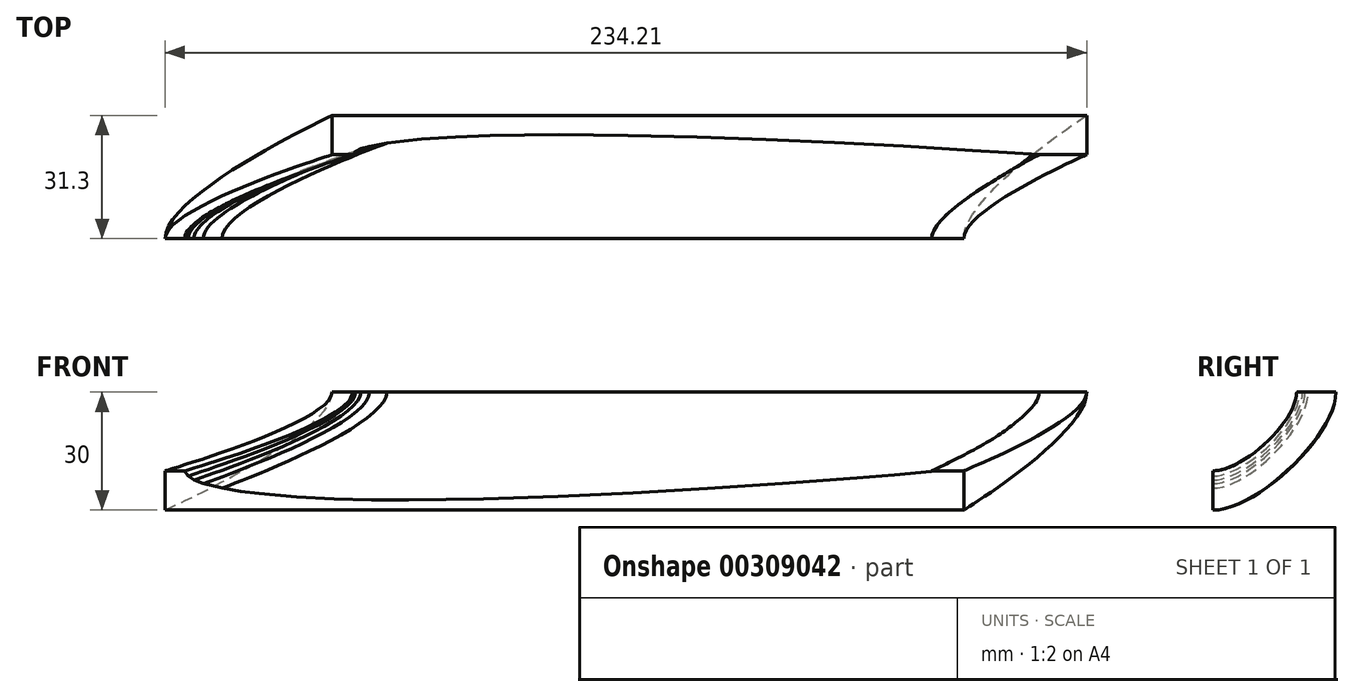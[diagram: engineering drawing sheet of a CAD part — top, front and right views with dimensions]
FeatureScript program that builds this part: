
annotation { "Feature Type Name" : "Feature", "Feature Type Description" : "" }
export const myFeature = defineFeature(function(context is Context, id is Id, definition is map)
    precondition{}
    {
        {
            var Q0;
            Q0=qCreatedBy(makeId("Top.planeOp"),FACE);
            cPlane(context, id + "F0", {"entities" : qUnion([Q0]), "cplaneType" : CPlaneType.OFFSET, "offset" : 20 * mm, "width" : 150 * mm, "height" : 150 * mm});
        }
        {
            var Q0;
            Q0=qCreatedBy(makeId("Front.planeOp"),FACE);
            var sketch = newSketch(context, id + "F1", { "sketchPlane" : qUnion([Q0])});
            skLineSegment(sketch, "E0", {"start": v(94.9, 0.16) * mm, "end": v(85.4, 1) * mm});
            skLineSegment(sketch, "E1", {"start": v(85.4, 1) * mm, "end": v(75.92, 1.8) * mm});
            skLineSegment(sketch, "E2", {"start": v(75.92, 1.8) * mm, "end": v(56.94, 3.25) * mm});
            skLineSegment(sketch, "E3", {"start": v(56.94, 3.25) * mm, "end": v(37.96, 4.54) * mm});
            skLineSegment(sketch, "E4", {"start": v(37.96, 4.54) * mm, "end": v(18.98, 5.66) * mm});
            skLineSegment(sketch, "E5", {"start": v(18.98, 5.66) * mm, "end": v(0, 6.56) * mm});
            skLineSegment(sketch, "E6", {"start": v(0, 6.56) * mm, "end": v(-18.98, 7.2) * mm});
            skLineSegment(sketch, "E7", {"start": v(-18.98, 7.2) * mm, "end": v(-37.96, 7.44) * mm});
            skLineSegment(sketch, "E8", {"start": v(-37.96, 7.44) * mm, "end": v(-47.45, 7.36) * mm});
            skLineSegment(sketch, "E9", {"start": v(-47.45, 7.36) * mm, "end": v(-56.94, 7.11) * mm});
            skLineSegment(sketch, "E10", {"start": v(-56.94, 7.11) * mm, "end": v(-66.43, 6.63) * mm});
            skLineSegment(sketch, "E11", {"start": v(-66.43, 6.63) * mm, "end": v(-75.92, 5.8) * mm});
            skLineSegment(sketch, "E12", {"start": v(-75.92, 5.8) * mm, "end": v(-80.66, 5.2) * mm});
            skLineSegment(sketch, "E13", {"start": v(-80.66, 5.2) * mm, "end": v(-85.4, 4.4) * mm});
            skLineSegment(sketch, "E14", {"start": v(-85.4, 4.4) * mm, "end": v(-90.15, 3.24) * mm});
            skLineSegment(sketch, "E15", {"start": v(-90.15, 3.24) * mm, "end": v(-92.52, 2.35) * mm});
            skLineSegment(sketch, "E16", {"start": v(-92.52, 2.35) * mm, "end": v(-94, 1.43) * mm});
            skLineSegment(sketch, "E17", {"start": v(-94, 1.43) * mm, "end": v(-94.9, 0) * mm});
            skLineSegment(sketch, "E18", {"start": v(-94.9, 0) * mm, "end": v(-94, -1.32) * mm});
            skLineSegment(sketch, "E19", {"start": v(-94, -1.32) * mm, "end": v(-92.52, -2.35) * mm});
            skLineSegment(sketch, "E20", {"start": v(-92.52, -2.35) * mm, "end": v(-90.15, -3.24) * mm});
            skLineSegment(sketch, "E21", {"start": v(-90.15, -3.24) * mm, "end": v(-85.4, -4.4) * mm});
            skLineSegment(sketch, "E22", {"start": v(-85.4, -4.4) * mm, "end": v(-80.66, -5.2) * mm});
            skLineSegment(sketch, "E23", {"start": v(-80.66, -5.2) * mm, "end": v(-75.92, -5.8) * mm});
            skLineSegment(sketch, "E24", {"start": v(-75.92, -5.8) * mm, "end": v(-66.43, -6.63) * mm});
            skLineSegment(sketch, "E25", {"start": v(-66.43, -6.63) * mm, "end": v(-56.94, -7.11) * mm});
            skLineSegment(sketch, "E26", {"start": v(-56.94, -7.11) * mm, "end": v(-47.45, -7.36) * mm});
            skLineSegment(sketch, "E27", {"start": v(-47.45, -7.36) * mm, "end": v(-37.96, -7.44) * mm});
            skLineSegment(sketch, "E28", {"start": v(-37.96, -7.44) * mm, "end": v(-18.98, -7.2) * mm});
            skLineSegment(sketch, "E29", {"start": v(-18.98, -7.2) * mm, "end": v(0, -6.56) * mm});
            skLineSegment(sketch, "E30", {"start": v(0, -6.56) * mm, "end": v(18.98, -5.66) * mm});
            skLineSegment(sketch, "E31", {"start": v(18.98, -5.66) * mm, "end": v(37.96, -4.54) * mm});
            skLineSegment(sketch, "E32", {"start": v(37.96, -4.54) * mm, "end": v(56.94, -3.25) * mm});
            skLineSegment(sketch, "E33", {"start": v(56.94, -3.25) * mm, "end": v(75.92, -1.8) * mm});
            skLineSegment(sketch, "E34", {"start": v(75.92, -1.8) * mm, "end": v(85.4, -1) * mm});
            skLineSegment(sketch, "E35", {"start": v(85.4, -1) * mm, "end": v(94.9, -0.16) * mm});
            skLineSegment(sketch, "E36", {"start": v(94.9, -0.16) * mm, "end": v(94.9, 0.16) * mm});
            skSolve(sketch);
        }
        {
            var Q0;
            Q0=qCreatedBy(id+"F0.planeOp",FACE);
            var sketch = newSketch(context, id + "F2", { "sketchPlane" : qUnion([Q0])});
            skLineSegment(sketch, "E37", {"start": v(122.76, 21.27) * mm, "end": v(114.01, 21.86) * mm});
            skLineSegment(sketch, "E38", {"start": v(114.01, 21.86) * mm, "end": v(105.26, 22.42) * mm});
            skLineSegment(sketch, "E39", {"start": v(105.26, 22.42) * mm, "end": v(87.76, 23.45) * mm});
            skLineSegment(sketch, "E40", {"start": v(87.76, 23.45) * mm, "end": v(70.26, 24.36) * mm});
            skLineSegment(sketch, "E41", {"start": v(70.26, 24.36) * mm, "end": v(52.76, 25.15) * mm});
            skLineSegment(sketch, "E42", {"start": v(52.76, 25.15) * mm, "end": v(35.26, 25.79) * mm});
            skLineSegment(sketch, "E43", {"start": v(35.26, 25.79) * mm, "end": v(17.76, 26.24) * mm});
            skLineSegment(sketch, "E44", {"start": v(17.76, 26.24) * mm, "end": v(0.26, 26.4) * mm});
            skLineSegment(sketch, "E45", {"start": v(0.26, 26.4) * mm, "end": v(-8.49, 26.36) * mm});
            skLineSegment(sketch, "E46", {"start": v(-8.49, 26.36) * mm, "end": v(-17.24, 26.18) * mm});
            skLineSegment(sketch, "E47", {"start": v(-17.24, 26.18) * mm, "end": v(-25.99, 25.83) * mm});
            skLineSegment(sketch, "E48", {"start": v(-25.99, 25.83) * mm, "end": v(-34.74, 25.25) * mm});
            skLineSegment(sketch, "E49", {"start": v(-34.74, 25.25) * mm, "end": v(-39.11, 24.83) * mm});
            skLineSegment(sketch, "E50", {"start": v(-39.11, 24.83) * mm, "end": v(-43.49, 24.27) * mm});
            skLineSegment(sketch, "E51", {"start": v(-43.49, 24.27) * mm, "end": v(-47.86, 23.44) * mm});
            skLineSegment(sketch, "E52", {"start": v(-47.86, 23.44) * mm, "end": v(-50.05, 22.81) * mm});
            skLineSegment(sketch, "E53", {"start": v(-50.05, 22.81) * mm, "end": v(-51.5, 22.08) * mm});
            skLineSegment(sketch, "E54", {"start": v(-51.5, 22.08) * mm, "end": v(-52.24, 21.16) * mm});
            skLineSegment(sketch, "E55", {"start": v(-52.24, 21.16) * mm, "end": v(-51.57, 20.22) * mm});
            skLineSegment(sketch, "E56", {"start": v(-51.57, 20.22) * mm, "end": v(-50.05, 19.5) * mm});
            skLineSegment(sketch, "E57", {"start": v(-50.05, 19.5) * mm, "end": v(-47.86, 18.87) * mm});
            skLineSegment(sketch, "E58", {"start": v(-47.86, 18.87) * mm, "end": v(-43.49, 18.05) * mm});
            skLineSegment(sketch, "E59", {"start": v(-43.49, 18.05) * mm, "end": v(-39.11, 17.48) * mm});
            skLineSegment(sketch, "E60", {"start": v(-39.11, 17.48) * mm, "end": v(-34.74, 17.06) * mm});
            skLineSegment(sketch, "E61", {"start": v(-34.74, 17.06) * mm, "end": v(-25.99, 16.48) * mm});
            skLineSegment(sketch, "E62", {"start": v(-25.99, 16.48) * mm, "end": v(-17.24, 16.14) * mm});
            skLineSegment(sketch, "E63", {"start": v(-17.24, 16.14) * mm, "end": v(-8.49, 15.96) * mm});
            skLineSegment(sketch, "E64", {"start": v(-8.49, 15.96) * mm, "end": v(0.26, 15.9) * mm});
            skLineSegment(sketch, "E65", {"start": v(0.26, 15.9) * mm, "end": v(17.76, 16.08) * mm});
            skLineSegment(sketch, "E66", {"start": v(17.76, 16.08) * mm, "end": v(35.26, 16.52) * mm});
            skLineSegment(sketch, "E67", {"start": v(35.26, 16.52) * mm, "end": v(52.76, 17.16) * mm});
            skLineSegment(sketch, "E68", {"start": v(52.76, 17.16) * mm, "end": v(70.26, 17.95) * mm});
            skLineSegment(sketch, "E69", {"start": v(70.26, 17.95) * mm, "end": v(87.76, 18.86) * mm});
            skLineSegment(sketch, "E70", {"start": v(87.76, 18.86) * mm, "end": v(105.26, 19.89) * mm});
            skLineSegment(sketch, "E71", {"start": v(105.26, 19.89) * mm, "end": v(114.01, 20.45) * mm});
            skLineSegment(sketch, "E72", {"start": v(114.01, 20.45) * mm, "end": v(122.76, 21.05) * mm});
            skLineSegment(sketch, "E73", {"start": v(122.76, 21.05) * mm, "end": v(122.76, 21.27) * mm});
            skSolve(sketch);
        }
        {
            var Q0;
            Q0=makeQuery(id+"F1.imprint","IMPRINT",FACE,{"disambiguationData":[TD([[makeQuery(id+"F1.imprint","IMPRINT",EDGE,{"derivedFrom":sQuery(id+"F1.wireOp",EDGE,"E0")}),1.0]])]});
            var Q1;
            Q1=makeQuery(id+"F2.imprint","IMPRINT",FACE,{"disambiguationData":[TD([[makeQuery(id+"F2.imprint","IMPRINT",EDGE,{"derivedFrom":sQuery(id+"F2.wireOp",EDGE,"E37")}),1.0]])]});
            loft(context, id + "F3", {"startCondition" : LoftEndDerivativeType.NORMAL_TO_PROFILE, "startMagnitude" : 1, "endCondition" : LoftEndDerivativeType.NORMAL_TO_PROFILE, "endMagnitude" : 1, "sheetProfilesArray" : [{ "sheetProfileEntities" : qUnion([Q0]) }, { "sheetProfileEntities" : qUnion([Q1]) }]});
        }
        {
            var Q0;
            Q0=qCreatedBy(makeId("Front.planeOp"),FACE);
            var sketch = newSketch(context, id + "F4", { "sketchPlane" : qUnion([Q0])});
            skLineSegment(sketch, "E74.bottom", {"start": v(-99.88, 0) * mm, "end": v(103.06, 0) * mm});
            skLineSegment(sketch, "E74.top", {"start": v(-99.88, -10) * mm, "end": v(103.06, -10) * mm});
            skLineSegment(sketch, "E74.left", {"start": v(-99.88, 0) * mm, "end": v(-99.88, -10) * mm});
            skLineSegment(sketch, "E74.right", {"start": v(103.06, 0) * mm, "end": v(103.06, -10) * mm});
            skSolve(sketch);
        }
        {
            var Q0;
            Q0=qCreatedBy(id+"F0.planeOp",FACE);
            var sketch = newSketch(context, id + "F5", { "sketchPlane" : qUnion([Q0])});
            skLineSegment(sketch, "E75.bottom", {"start": v(-57.39, 21.3) * mm, "end": v(134.33, 21.3) * mm});
            skLineSegment(sketch, "E75.top", {"start": v(-57.39, 31.3) * mm, "end": v(134.33, 31.3) * mm});
            skLineSegment(sketch, "E75.left", {"start": v(-57.39, 21.3) * mm, "end": v(-57.39, 31.3) * mm});
            skLineSegment(sketch, "E75.right", {"start": v(134.33, 21.3) * mm, "end": v(134.33, 31.3) * mm});
            skSolve(sketch);
        }
        {
            var Q1;
            Q1=makeQuery(id+"F4.imprint","IMPRINT",FACE,{"disambiguationData":[TD([[makeQuery(id+"F4.imprint","IMPRINT",EDGE,{"derivedFrom":sQuery(id+"F4.wireOp",EDGE,"E74.bottom")}),-1.0]])]});
            var Q2;
            Q2=makeQuery(id+"F5.imprint","IMPRINT",FACE,{"disambiguationData":[TD([[makeQuery(id+"F5.imprint","IMPRINT",EDGE,{"derivedFrom":sQuery(id+"F5.wireOp",EDGE,"E75.bottom")}),1.0]])]});
            loft(context, id + "F6", {"startCondition" : LoftEndDerivativeType.NORMAL_TO_PROFILE, "startMagnitude" : 1, "endCondition" : LoftEndDerivativeType.NORMAL_TO_PROFILE, "endMagnitude" : 1, "sheetProfilesArray" : [{ "sheetProfileEntities" : qUnion([Q1]) }, { "sheetProfileEntities" : qUnion([Q2]) }]});
        }
        {
            var Q0;
            Q0=makeQuery(id+"F3.opLoft","SWEPT_BODY",BODY,{"disambiguationData":[OSD([makeQuery(id+"F1.imprint","IMPRINT",FACE,{"disambiguationData":[TD([[makeQuery(id+"F1.imprint","IMPRINT",EDGE,{"derivedFrom":sQuery(id+"F1.wireOp",EDGE,"E0")}),1.0]])]}),makeQuery(id+"F2.imprint","IMPRINT",FACE,{"disambiguationData":[TD([[makeQuery(id+"F2.imprint","IMPRINT",EDGE,{"derivedFrom":sQuery(id+"F2.wireOp",EDGE,"E37")}),1.0]])]})])]});
            var Q1;
            Q1=makeQuery(id+"F6.opLoft","SWEPT_BODY",BODY,{"disambiguationData":[OSD([makeQuery(id+"F4.imprint","IMPRINT",FACE,{"disambiguationData":[TD([[makeQuery(id+"F4.imprint","IMPRINT",EDGE,{"derivedFrom":sQuery(id+"F4.wireOp",EDGE,"E74.bottom")}),-1.0]])]}),makeQuery(id+"F5.imprint","IMPRINT",FACE,{"disambiguationData":[TD([[makeQuery(id+"F5.imprint","IMPRINT",EDGE,{"derivedFrom":sQuery(id+"F5.wireOp",EDGE,"E75.bottom")}),1.0]])]})])]});
            booleanBodies(context, id + "F7", {"operationType" : BooleanOperationType.SUBTRACTION, "tools" : qUnion([Q0]), "targets" : qUnion([Q1])});
        }
    });
